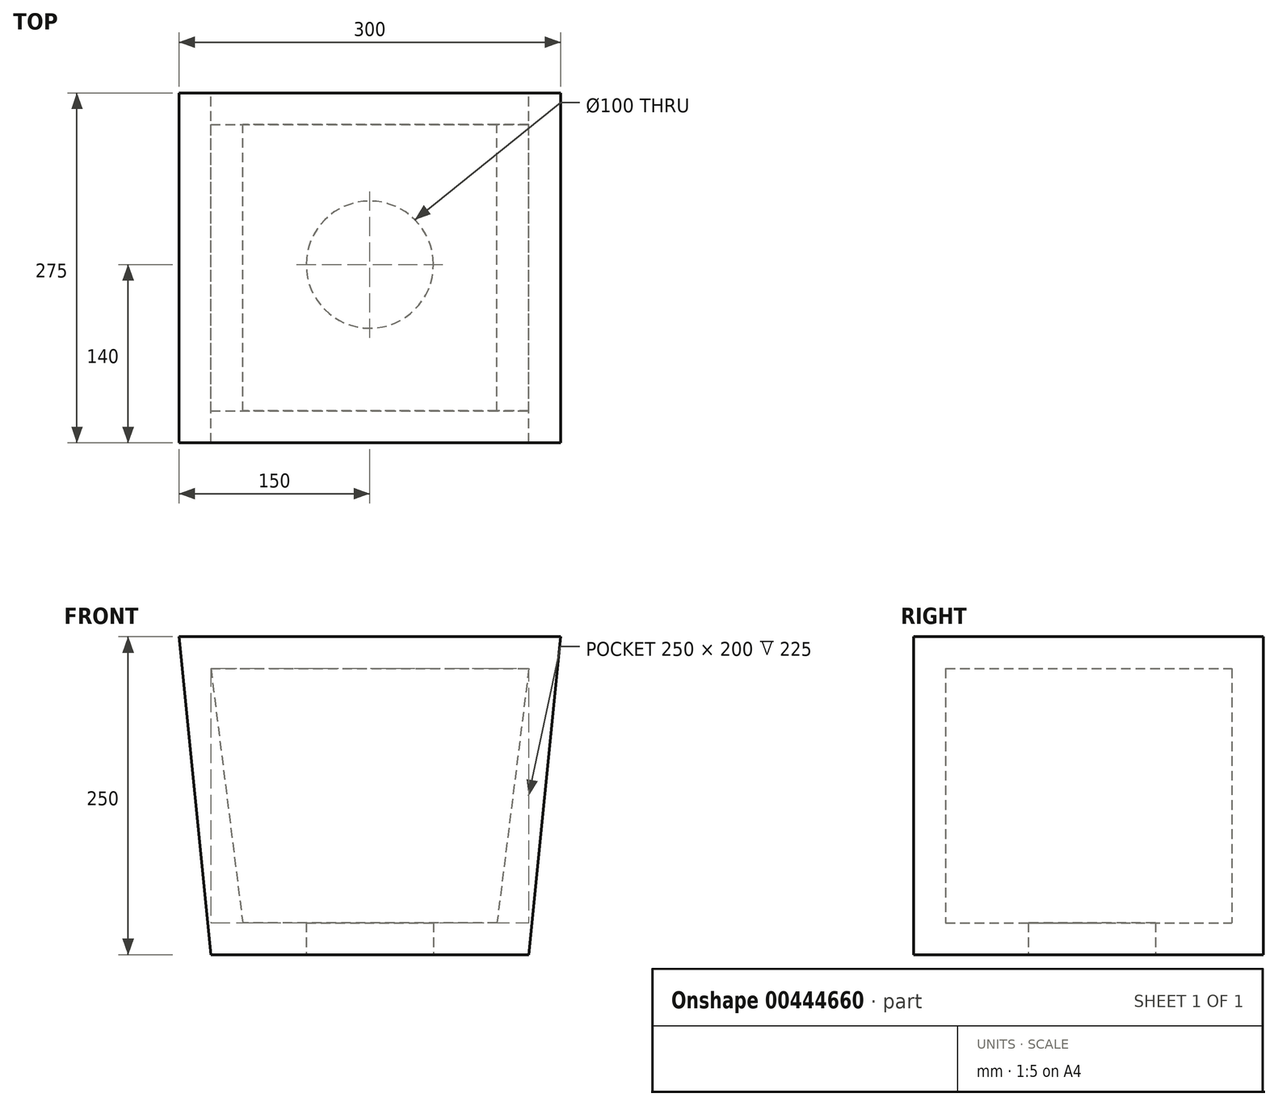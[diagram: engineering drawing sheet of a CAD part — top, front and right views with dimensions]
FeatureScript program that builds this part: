
annotation { "Feature Type Name" : "Feature", "Feature Type Description" : "" }
export const myFeature = defineFeature(function(context is Context, id is Id, definition is map)
    precondition{}
    {
        {
            var Q0;
            Q0=qCreatedBy(makeId("Front.planeOp"),FACE);
            var sketch = newSketch(context, id + "F0", { "sketchPlane" : qUnion([Q0])});
            skLineSegment(sketch, "E0.bottom", {"start": v(125, -125) * mm, "end": v(-125, -125) * mm});
            skPoint(sketch, "E0.middle", {"position": v(0, 0) * mm});
            skLineSegment(sketch, "E1", {"start": v(-150, 125) * mm, "end": v(-125, -125) * mm});
            skLineSegment(sketch, "E2", {"start": v(125, -125) * mm, "end": v(150, 125) * mm});
            skLineSegment(sketch, "E3", {"start": v(-150, 125) * mm, "end": v(150, 125) * mm});
            skLineSegment(sketch, "E4.bottom", {"start": v(100, -100) * mm, "end": v(-100, -100) * mm});
            skLineSegment(sketch, "E5", {"start": v(-125, 100) * mm, "end": v(-100, -100) * mm});
            skLineSegment(sketch, "E6", {"start": v(125, 100) * mm, "end": v(100, -100) * mm});
            skLineSegment(sketch, "E7", {"start": v(-125, 100) * mm, "end": v(125, 100) * mm});
            skSolve(sketch);
        }
        {
            var Q0;
            Q0=makeQuery(id+"F0.imprint","IMPRINT",FACE,{"disambiguationData":[TD([[makeQuery(id+"F0.imprint","IMPRINT",EDGE,{"derivedFrom":sQuery(id+"F0.wireOp",EDGE,"E0.bottom")}),-1.0]])]});
            extrude(context, id + "F1", {"entities" : qUnion([Q0]), "depth" : 225 * mm});
        }
        {
            var Q0;
            Q0=makeQuery(id+"F1.opExtrude","CAP_FACE",FACE,{"disambiguationData":[OSD([sQuery(id+"F0.wireOp",EDGE,"E0.bottom"),sQuery(id+"F0.wireOp",EDGE,"E1"),sQuery(id+"F0.wireOp",EDGE,"E2"),sQuery(id+"F0.wireOp",EDGE,"E3"),sQuery(id+"F0.wireOp",EDGE,"E4.bottom"),sQuery(id+"F0.wireOp",EDGE,"E5"),sQuery(id+"F0.wireOp",EDGE,"E6"),sQuery(id+"F0.wireOp",EDGE,"E7")])],"isStart":false});
            var sketch = newSketch(context, id + "F2", { "sketchPlane" : qUnion([Q0])});
            skLineSegment(sketch, "E8", {"start": v(-125, 100) * mm, "end": v(125, 100) * mm});
            skLineSegment(sketch, "E9", {"start": v(125, 100) * mm, "end": v(100, -100) * mm});
            skLineSegment(sketch, "E10", {"start": v(100, -100) * mm, "end": v(-100, -100) * mm});
            skLineSegment(sketch, "E11", {"start": v(-100, -100) * mm, "end": v(-125, 100) * mm});
            skSolve(sketch);
        }
        {
            var Q0;
            Q0=makeQuery(id+"F2.imprint","IMPRINT",FACE,{"disambiguationData":[TD([[makeQuery(id+"F2.imprint","IMPRINT",EDGE,{"derivedFrom":sQuery(id+"F2.wireOp",EDGE,"E8")}),1.0]])]});
            var sketch = newSketch(context, id + "F3", { "sketchPlane" : qUnion([Q0])});
            skLineSegment(sketch, "E12.top", {"start": v(150, 125) * mm, "end": v(-150, 125) * mm});
            skPoint(sketch, "E12.middle", {"position": v(0, 0) * mm});
            skLineSegment(sketch, "E13.bottom", {"start": v(125, -125) * mm, "end": v(-125, -125) * mm});
            skLineSegment(sketch, "E14", {"start": v(-150, 125) * mm, "end": v(-125, -125) * mm});
            skLineSegment(sketch, "E15", {"start": v(125, -125) * mm, "end": v(150, 125) * mm});
            skSolve(sketch);
        }
        {
            var Q0;
            Q0 = qSketchRegion(id + "F3", true);
            var Q1;
            Q1=makeQuery(id+"F2.imprint","IMPRINT",FACE,{"disambiguationData":[TD([[makeQuery(id+"F2.imprint","IMPRINT",EDGE,{"derivedFrom":sQuery(id+"F2.wireOp",EDGE,"E8")}),1.0]])]});
            extrude(context, id + "F4", {"entities" : qUnion([Q0, Q1]), "operationType" : NewBodyOperationType.ADD, "depth" : 25 * mm});
        }
        {
            var Q0;
            Q0=makeQuery(id+"F1.opExtrude","CAP_FACE",FACE,{"disambiguationData":[OSD([sQuery(id+"F0.wireOp",EDGE,"E0.bottom"),sQuery(id+"F0.wireOp",EDGE,"E1"),sQuery(id+"F0.wireOp",EDGE,"E2"),sQuery(id+"F0.wireOp",EDGE,"E3"),sQuery(id+"F0.wireOp",EDGE,"E4.bottom"),sQuery(id+"F0.wireOp",EDGE,"E5"),sQuery(id+"F0.wireOp",EDGE,"E6"),sQuery(id+"F0.wireOp",EDGE,"E7")])],"isStart":true});
            var sketch = newSketch(context, id + "F5", { "sketchPlane" : qUnion([Q0])});
            skLineSegment(sketch, "E16.top", {"start": v(150, 125) * mm, "end": v(-150, 125) * mm});
            skPoint(sketch, "E16.middle", {"position": v(0, 0) * mm});
            skLineSegment(sketch, "E17.bottom", {"start": v(125, -125) * mm, "end": v(-125, -125) * mm});
            skLineSegment(sketch, "E18", {"start": v(-150, 125) * mm, "end": v(-125, -125) * mm});
            skLineSegment(sketch, "E19", {"start": v(125, -125) * mm, "end": v(150, 125) * mm});
            skSolve(sketch);
        }
        {
            var Q0;
            Q0 = qSketchRegion(id + "F5", true);
            extrude(context, id + "F6", {"entities" : qUnion([Q0]), "operationType" : NewBodyOperationType.ADD, "depth" : 25 * mm});
        }
        {
            var Q0;
            {var subQ0=sQuery(id+"F0.wireOp",EDGE,"E0.bottom");Q0=makeQuery(id+"F6.boolean.opBoolean","MERGE",FACE,{"derivedFrom":[makeQuery(id+"F4.boolean.opBoolean","MERGE",FACE,{"derivedFrom":[makeQuery(id+"F1.opExtrude","SWEPT_FACE",FACE,{"disambiguationData":[OSD([subQ0])]}),makeQuery(id+"F4.opExtrude","SWEPT_FACE",FACE,{"disambiguationData":[OSD([subQ0])]})]}),makeQuery(id+"F6.opExtrude","SWEPT_FACE",FACE,{"disambiguationData":[OSD([sQuery(id+"F5.wireOp",EDGE,"E17.bottom")])]})]});}
            var sketch = newSketch(context, id + "F7", { "sketchPlane" : qUnion([Q0])});
            skCircle(sketch, "E20", {"center": v(0, 110) * mm, "radius": 50 * mm});
            skSolve(sketch);
        }
        {
            var Q0;
            Q0=makeQuery(id+"F7.imprint","IMPRINT",FACE,{"disambiguationData":[TD([[makeQuery(id+"F7.imprint","IMPRINT",EDGE,{"derivedFrom":sQuery(id+"F7.wireOp",EDGE,"E20")}),1.0]])]});
            extrude(context, id + "F8", {"entities" : qUnion([Q0]), "operationType" : NewBodyOperationType.REMOVE, "oppositeDirection" : true, "depth" : 25 * mm});
        }
    });
